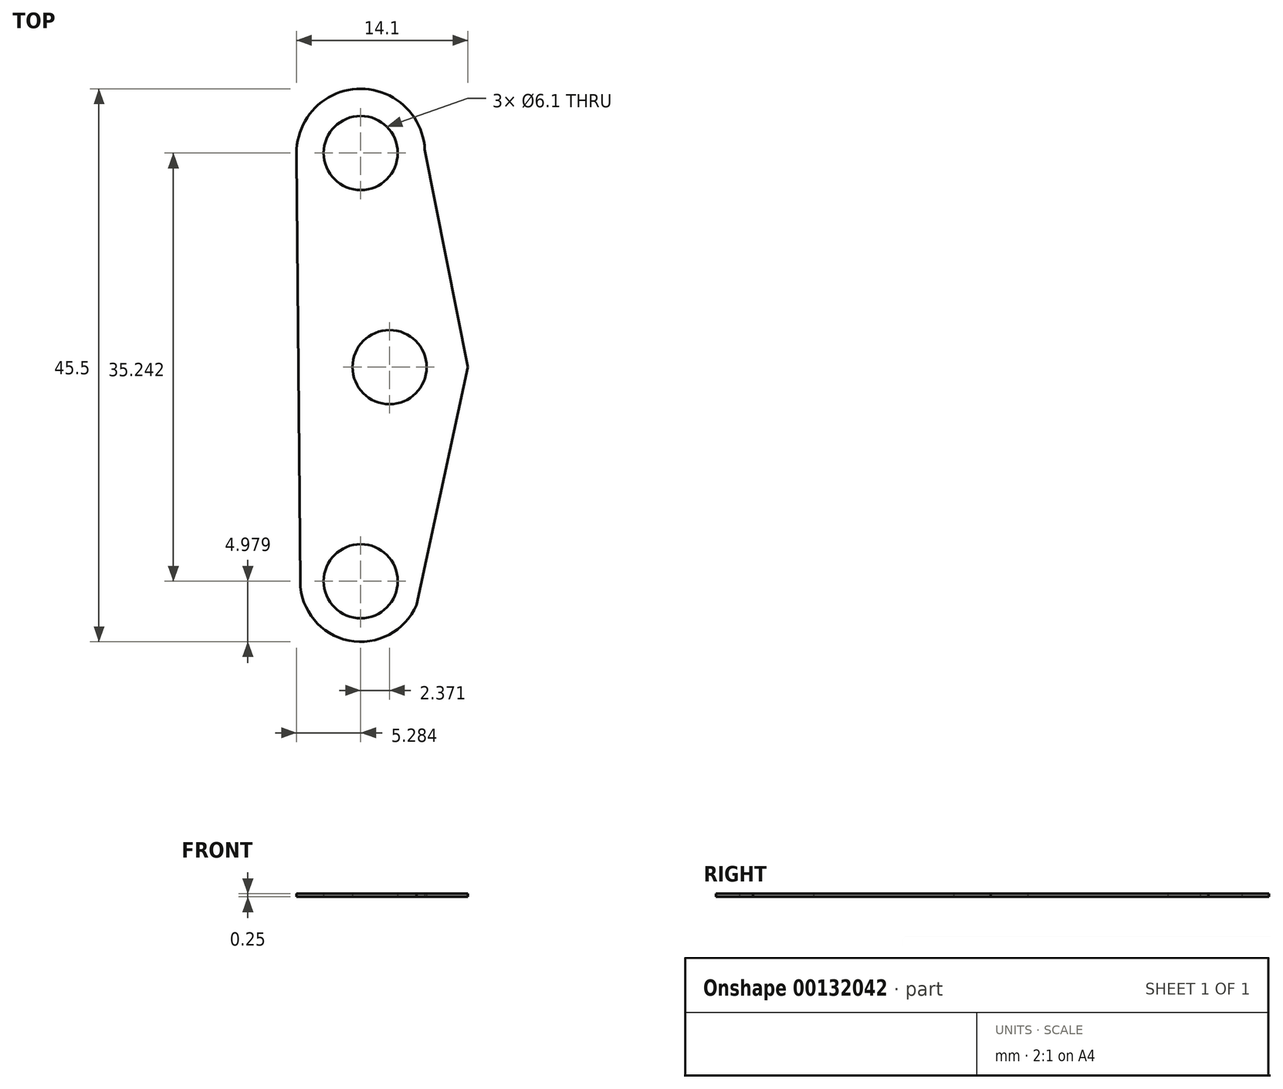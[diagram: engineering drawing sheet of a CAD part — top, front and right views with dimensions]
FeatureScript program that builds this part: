
annotation { "Feature Type Name" : "Feature", "Feature Type Description" : "" }
export const myFeature = defineFeature(function(context is Context, id is Id, definition is map)
    precondition{}
    {
        {
            var Q0;
            Q0=qCreatedBy(makeId("Top.planeOp"),FACE);
            var sketch = newSketch(context, id + "F0", { "sketchPlane" : qUnion([Q0])});
            skCircle(sketch, "E0", {"center": v(66.68, 0) * mm, "radius": 3.05 * mm});
            skCircle(sketch, "E1", {"center": v(64.3, 17.62) * mm, "radius": 3.05 * mm});
            skCircle(sketch, "E2", {"center": v(64.3, -17.62) * mm, "radius": 3.05 * mm});
            skPoint(sketch, "E3.center.orphan", {"position": v(0, 0) * mm});
            skArc(sketch, "E4", {"start": v(69.58, 17.9) * mm, "mid": v(63.97, 22.9) * mm, "end": v(59.04, 17.24) * mm});
            skArc(sketch, "E5", {"start": v(59.33, -17.66) * mm, "mid": v(63.33, -22.5) * mm, "end": v(68.88, -19.57) * mm});
            skLineSegment(sketch, "E6", {"start": v(59.04, 17.24) * mm, "end": v(59.33, -17.66) * mm});
            skLineSegment(sketch, "E7", {"start": v(69.58, 17.9) * mm, "end": v(73.12, 0) * mm});
            skLineSegment(sketch, "E8", {"start": v(73.12, 0) * mm, "end": v(68.88, -19.57) * mm});
            skSolve(sketch);
        }
        {
            var Q0;
            Q0 = qSketchRegion(id + "F0", true);
            extrude(context, id + "F1", {"entities" : qUnion([Q0]), "depth" : 0.25 * mm});
        }
    });
